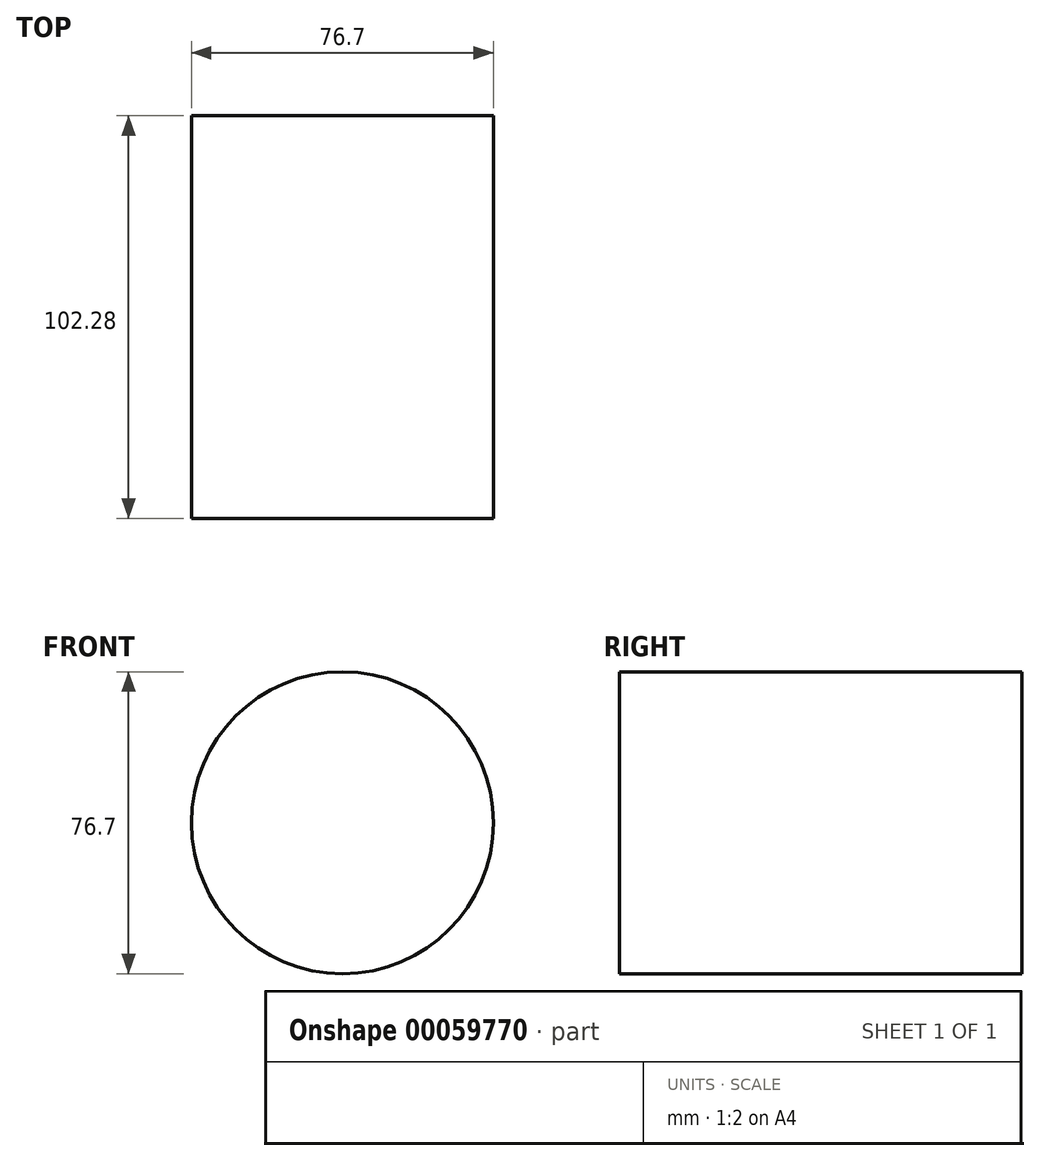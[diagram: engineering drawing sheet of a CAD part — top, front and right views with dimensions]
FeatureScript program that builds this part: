
annotation { "Feature Type Name" : "Feature", "Feature Type Description" : "" }
export const myFeature = defineFeature(function(context is Context, id is Id, definition is map)
    precondition{}
    {
        {
            var Q0;
            Q0=qCreatedBy(makeId("Front.planeOp"),FACE);
            var sketch = newSketch(context, id + "F0", { "sketchPlane" : qUnion([Q0])});
            skCircle(sketch, "E0", {"center": v(0, 0) * mm, "radius": 38.35 * mm});
            skSolve(sketch);
        }
        {
            var Q0;
            Q0 = qSketchRegion(id + "F0", true);
            extrude(context, id + "F1", {"entities" : qUnion([Q0]), "depth" : 102.28 * mm});
        }
    });
